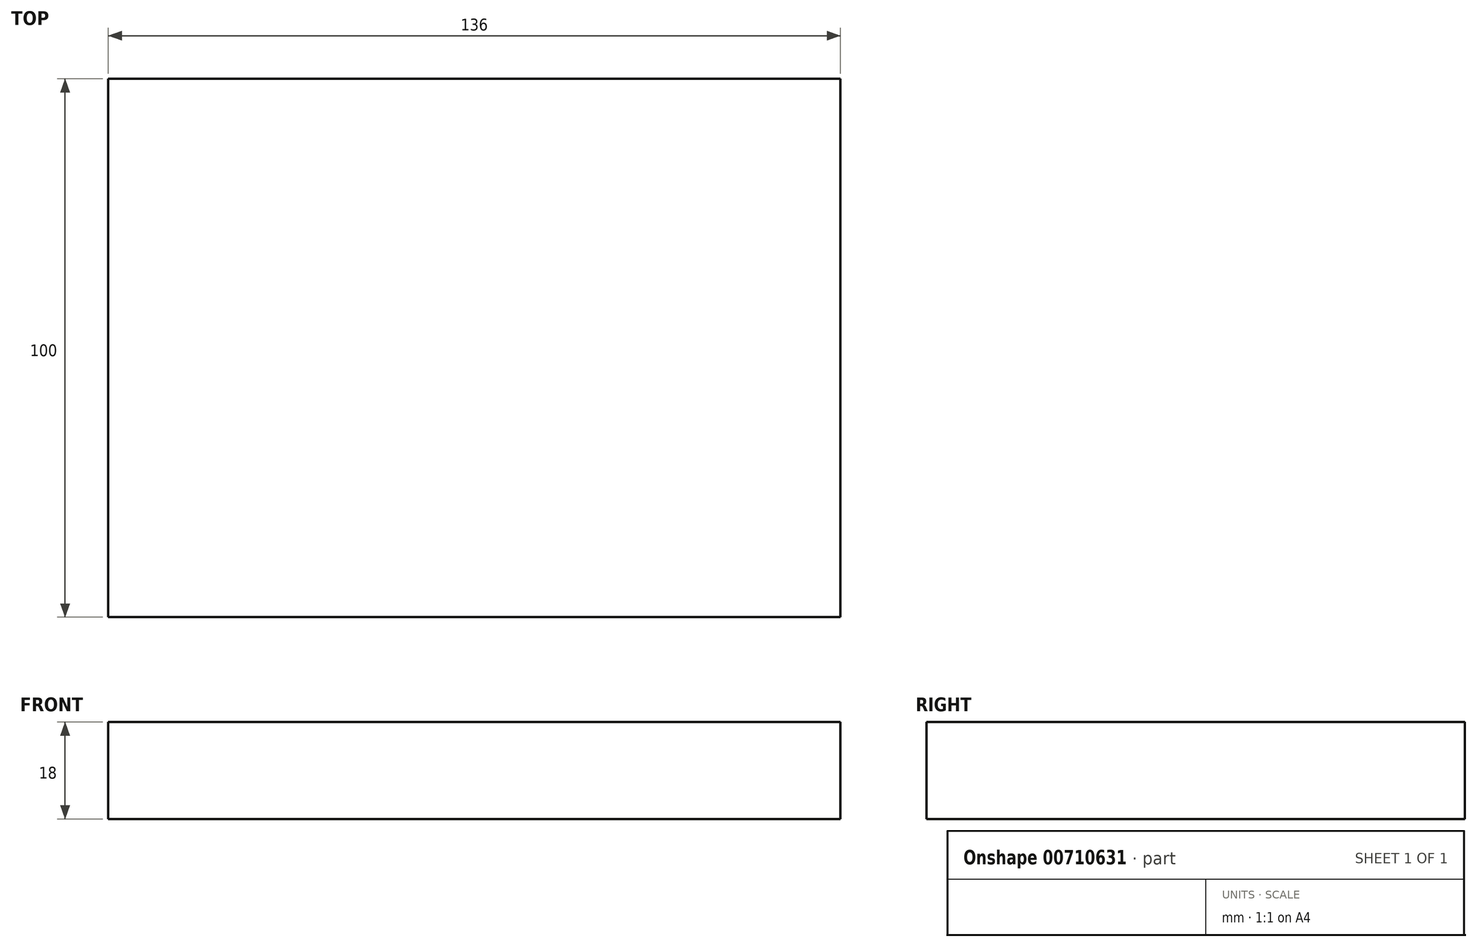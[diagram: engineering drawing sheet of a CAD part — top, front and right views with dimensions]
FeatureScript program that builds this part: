
annotation { "Feature Type Name" : "Feature", "Feature Type Description" : "" }
export const myFeature = defineFeature(function(context is Context, id is Id, definition is map)
    precondition{}
    {
        {
            var Q0;
            Q0=qCreatedBy(makeId("Top.planeOp"),FACE);
            var sketch = newSketch(context, id + "F0", { "sketchPlane" : qUnion([Q0])});
            skLineSegment(sketch, "E0.bottom", {"start": v(0, 0) * mm, "end": v(136, 0) * mm});
            skLineSegment(sketch, "E0.top", {"start": v(0, 100) * mm, "end": v(136, 100) * mm});
            skLineSegment(sketch, "E0.left", {"start": v(0, 0) * mm, "end": v(0, 100) * mm});
            skLineSegment(sketch, "E0.right", {"start": v(136, 0) * mm, "end": v(136, 100) * mm});
            skSolve(sketch);
        }
        {
            var Q0;
            Q0=makeQuery(id+"F0.imprint","IMPRINT",FACE,{"disambiguationData":[TD([[makeQuery(id+"F0.imprint","IMPRINT",EDGE,{"derivedFrom":sQuery(id+"F0.wireOp",EDGE,"E0.bottom")}),1.0]])]});
            extrude(context, id + "F1", {"entities" : qUnion([Q0]), "depth" : 18 * mm, "offsetDistance" : 25 * mm});
        }
    });
